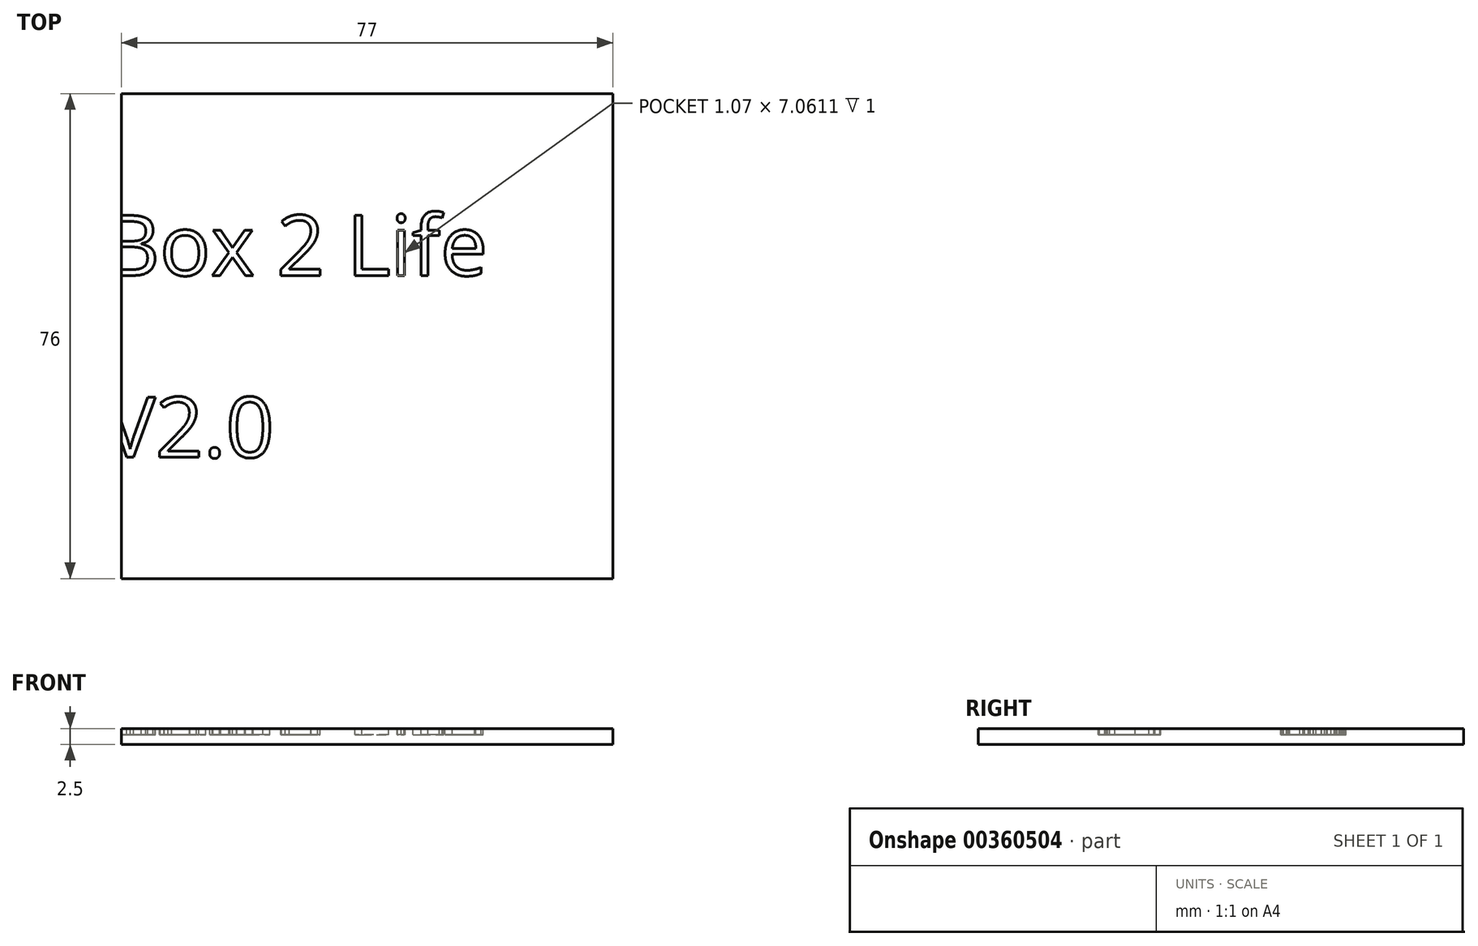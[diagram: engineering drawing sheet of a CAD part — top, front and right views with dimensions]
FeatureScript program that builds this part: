
annotation { "Feature Type Name" : "Feature", "Feature Type Description" : "" }
export const myFeature = defineFeature(function(context is Context, id is Id, definition is map)
    precondition{}
    {
        {
            var Q0;
            Q0=qCreatedBy(makeId("Top.planeOp"),FACE);
            var sketch = newSketch(context, id + "F0", { "sketchPlane" : qUnion([Q0])});
            skLineSegment(sketch, "E0.bottom", {"start": v(0, 0) * mm, "end": v(77, 0) * mm});
            skLineSegment(sketch, "E0.top", {"start": v(0, 76) * mm, "end": v(77, 76) * mm});
            skLineSegment(sketch, "E0.left", {"start": v(0, 0) * mm, "end": v(0, 76) * mm});
            skLineSegment(sketch, "E0.right", {"start": v(77, 0) * mm, "end": v(77, 76) * mm});
            skSolve(sketch);
        }
        {
            var Q0;
            Q0=qSketchRegion(id+"F0",true);
            extrude(context, id + "F1", {"entities" : qUnion([Q0]), "depth" : 2.5 * mm});
        }
        {
            var Q0;
            Q0=makeQuery(id+"F1.opExtrude","CAP_FACE",FACE,{"disambiguationData":[OSD([sQuery(id+"F0.wireOp",EDGE,"E0.bottom"),sQuery(id+"F0.wireOp",EDGE,"E0.top"),sQuery(id+"F0.wireOp",EDGE,"E0.left"),sQuery(id+"F0.wireOp",EDGE,"E0.right")])],"isStart":false});
            var sketch = newSketch(context, id + "F2", { "sketchPlane" : qUnion([Q0])});
            skText(sketch, "E1", { "text": "Box 2 Life", "fontName": "OpenSans-Regular.ttf"});
            skText(sketch, "E2", { "text": "V2.0", "fontName": "OpenSans-Regular.ttf"});
            skLineSegment(sketch, "E3", {"start": v(38.5, 57) * mm, "end": v(38.5, 76) * mm, "construction": true});
            const initialGuessF2  = {"E1": [-0.00253, 0.0475, 1, 0, 0.0095], "E2": [-0.00253, 0.019, 1, 0, 0.0095]};
            skSetInitialGuess(sketch, initialGuessF2);
            skSolve(sketch);
        }
        {
            var Q0;
            Q0=qSketchRegion(id+"F2",true);
            extrude(context, id + "F3", {"entities" : qUnion([Q0]), "operationType" : NewBodyOperationType.REMOVE, "oppositeDirection" : true, "depth" : 1 * mm});
        }
    });
